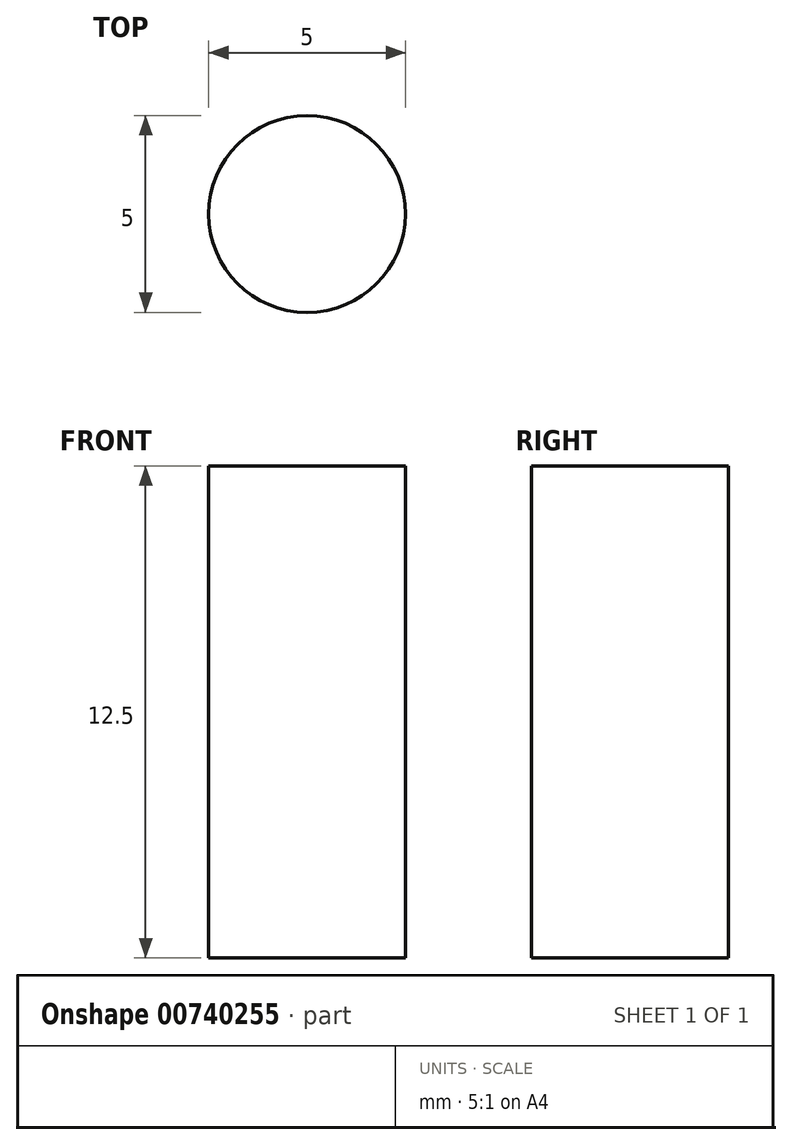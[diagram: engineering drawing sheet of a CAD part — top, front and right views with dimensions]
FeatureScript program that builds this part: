
annotation { "Feature Type Name" : "Feature", "Feature Type Description" : "" }
export const myFeature = defineFeature(function(context is Context, id is Id, definition is map)
    precondition{}
    {
        {
            var Q0;
            Q0=qCreatedBy(makeId("Top.planeOp"),FACE);
            var sketch = newSketch(context, id + "F0", { "sketchPlane" : qUnion([Q0])});
            skCircle(sketch, "E0", {"center": v(0, 0) * mm, "radius": 2.5 * mm});
            skCircle(sketch, "E1", {"center": v(0, 0) * mm, "radius": 1.59 * mm});
            skLineSegment(sketch, "E2", {"start": v(0, 1.59) * mm, "end": v(0, -1.08) * mm, "construction": true});
            skLineSegment(sketch, "E3", {"start": v(-2.25, -1.08) * mm, "end": v(2.25, -1.08) * mm});
            skSolve(sketch);
        }
        {
            var Q0;
            Q0 = qSketchRegion(id + "F0", true);
            var Q1;
            {var subQ0=sQuery(id+"F0.wireOp",EDGE,"E3");var subQ1=sQuery(id+"F0.wireOp",EDGE,"E1");var subQ2=makeQuery(id+"F0.imprint","INTERSECT",VERTEX,{"disambiguationData":[OD(0.0)],"derivedFrom":[subQ1,subQ0]});Q1=makeQuery(id+"F0.imprint","IMPRINT",FACE,{"disambiguationData":[TD([[makeQuery(id+"F0.imprint","IMPRINT",EDGE,{"disambiguationData":[TD([[subQ2,1.0]])],"derivedFrom":subQ1}),1.0]])]});}
            var Q2;
            {var subQ0=sQuery(id+"F0.wireOp",EDGE,"E3");var subQ1=sQuery(id+"F0.wireOp",EDGE,"E1");var subQ2=makeQuery(id+"F0.imprint","INTERSECT",VERTEX,{"disambiguationData":[OD(0.0)],"derivedFrom":[subQ1,subQ0]});Q2=makeQuery(id+"F0.imprint","IMPRINT",FACE,{"disambiguationData":[TD([[makeQuery(id+"F0.imprint","IMPRINT",EDGE,{"disambiguationData":[TD([[subQ2,-1.0]])],"derivedFrom":subQ1}),1.0]])]});}
            extrude(context, id + "F1", {"entities" : qUnion([Q0, Q1, Q2]), "depth" : 12.5 * mm, "offsetDistance" : 25 * mm});
        }
    });
